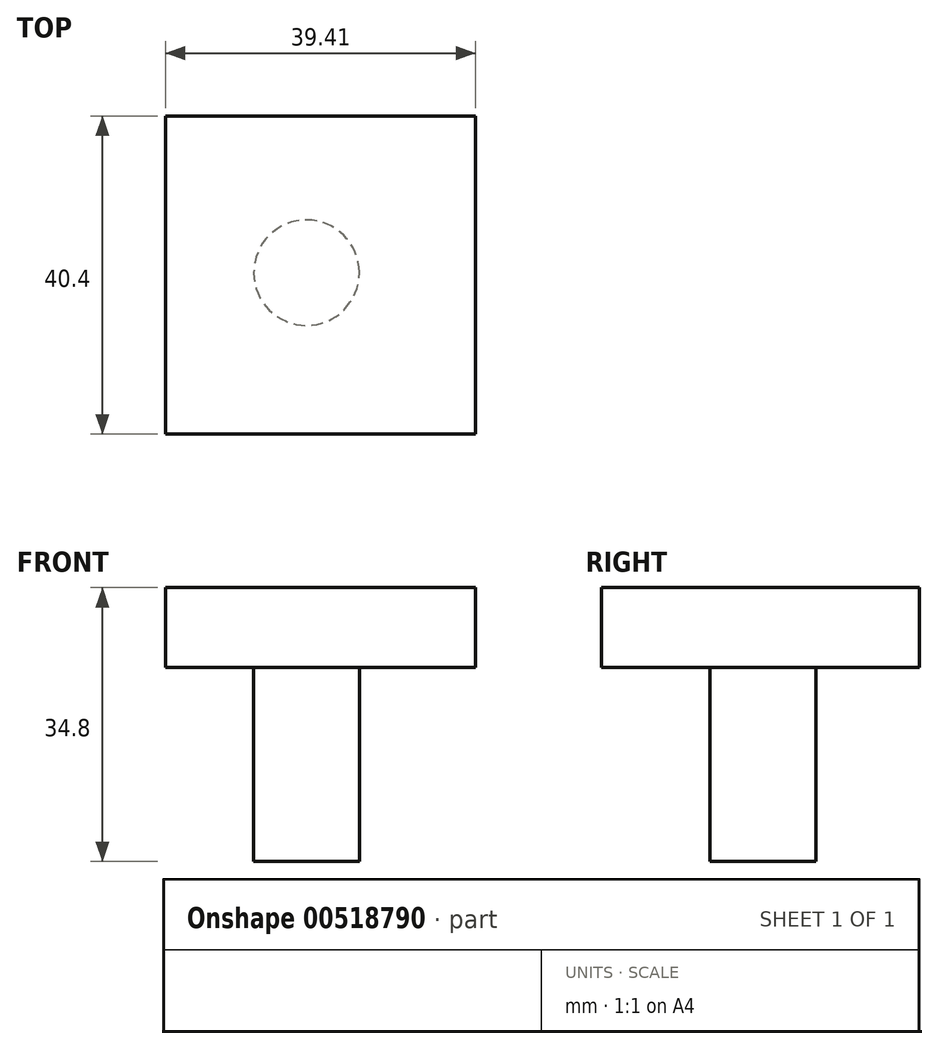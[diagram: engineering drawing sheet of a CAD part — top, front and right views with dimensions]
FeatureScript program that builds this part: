
annotation { "Feature Type Name" : "Feature", "Feature Type Description" : "" }
export const myFeature = defineFeature(function(context is Context, id is Id, definition is map)
    precondition{}
    {
        {
            var Q0;
            Q0=qCreatedBy(makeId("Top.planeOp"),FACE);
            var sketch = newSketch(context, id + "F0", { "sketchPlane" : qUnion([Q0])});
            skLineSegment(sketch, "E0.bottom", {"start": v(-17.93, 19.9) * mm, "end": v(21.48, 19.9) * mm});
            skLineSegment(sketch, "E0.top", {"start": v(-17.93, -20.5) * mm, "end": v(21.48, -20.5) * mm});
            skLineSegment(sketch, "E0.left", {"start": v(-17.93, 19.9) * mm, "end": v(-17.93, -20.5) * mm});
            skLineSegment(sketch, "E0.right", {"start": v(21.48, 19.9) * mm, "end": v(21.48, -20.5) * mm});
            skSolve(sketch);
        }
        {
            var Q0;
            Q0=makeQuery(id+"F0.imprint","IMPRINT",FACE,{"disambiguationData":[TD([[makeQuery(id+"F0.imprint","IMPRINT",EDGE,{"derivedFrom":sQuery(id+"F0.wireOp",EDGE,"E0.bottom")}),-1.0]])]});
            var sketch = newSketch(context, id + "F1", { "sketchPlane" : qUnion([Q0])});
            skCircle(sketch, "E1", {"center": v(0, 0) * mm, "radius": 6.7 * mm});
            skSolve(sketch);
        }
        {
            var Q0;
            Q0=makeQuery(id+"F0.imprint","IMPRINT",FACE,{"disambiguationData":[TD([[makeQuery(id+"F0.imprint","IMPRINT",EDGE,{"derivedFrom":sQuery(id+"F0.wireOp",EDGE,"E0.bottom")}),-1.0]])]});
            extrude(context, id + "F2", {"entities" : qUnion([Q0]), "depth" : 10.16 * mm});
        }
        {
            var Q0;
            Q0=makeQuery(id+"F2.opExtrude","CAP_FACE",FACE,{"disambiguationData":[OSD([sQuery(id+"F0.wireOp",EDGE,"E0.bottom"),sQuery(id+"F0.wireOp",EDGE,"E0.top"),sQuery(id+"F0.wireOp",EDGE,"E0.left"),sQuery(id+"F0.wireOp",EDGE,"E0.right")])],"isStart":false});
            var sketch = newSketch(context, id + "F3", { "sketchPlane" : qUnion([Q0])});
            skSolve(sketch);
        }
        {
            var Q0;
            Q0 = qSketchRegion(id + "F3", true);
            var Q1;
            Q1=makeQuery(id+"F3.imprint","IMPRINT",FACE,{"disambiguationData":[TD([[makeQuery(id+"F3.imprint","IMPRINT",EDGE,{"derivedFrom":makeQuery(id+"F2.opExtrude","CAP_EDGE",EDGE,{"disambiguationData":[OSD([sQuery(id+"F0.wireOp",EDGE,"E0.bottom")])],"isStart":false})}),-1.0]])]});
            var Q2;
            Q2 = qSketchRegion(id + "F1", true);
            extrude(context, id + "F4", {"entities" : qUnion([Q0, Q1, Q2]), "operationType" : NewBodyOperationType.ADD, "oppositeDirection" : true, "depth" : 24.64 * mm});
        }
    });
